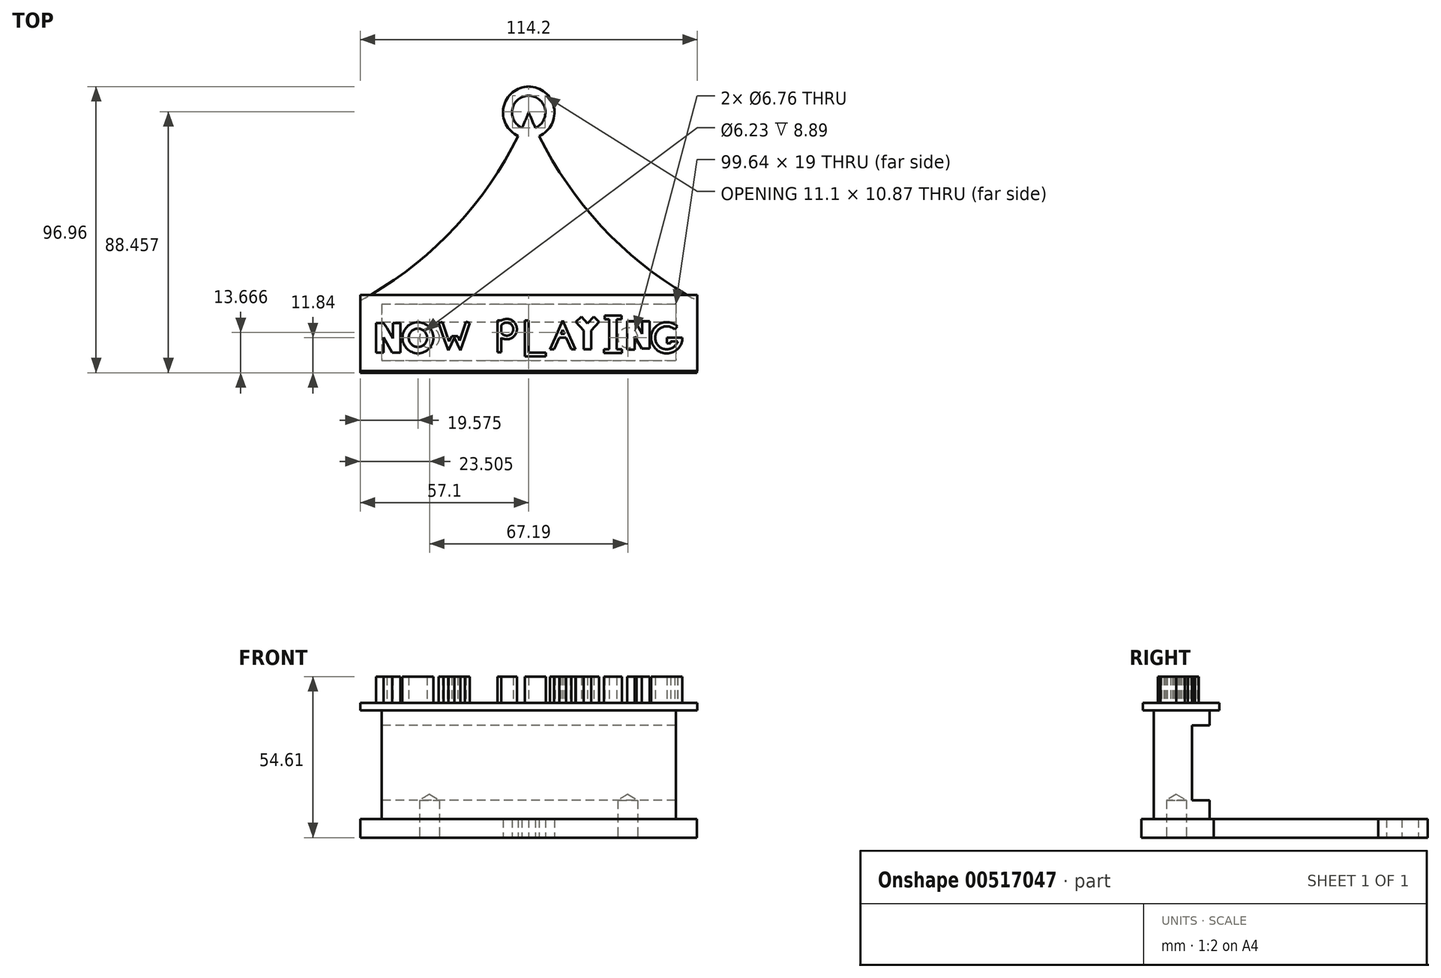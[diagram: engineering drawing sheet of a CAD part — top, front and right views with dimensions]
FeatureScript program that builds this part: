
annotation { "Feature Type Name" : "Feature", "Feature Type Description" : "" }
export const myFeature = defineFeature(function(context is Context, id is Id, definition is map)
    precondition{}
    {
        {
            var Q0;
            Q0=qCreatedBy(makeId("Top.planeOp"),FACE);
            var sketch = newSketch(context, id + "F0", { "sketchPlane" : qUnion([Q0])});
            skLineSegment(sketch, "E0", {"start": v(0, 0) * mm, "end": v(0, 12.6) * mm});
            skLineSegment(sketch, "E1", {"start": v(57, 12.6) * mm, "end": v(57, -11.84) * mm});
            skLineSegment(sketch, "E2", {"start": v(57, -11.84) * mm, "end": v(0, -11.84) * mm});
            skLineSegment(sketch, "E3", {"start": v(0, -11.84) * mm, "end": v(0, 0) * mm});
            skLineSegment(sketch, "E4.MirrorCS", {"start": v(-57, 12.6) * mm, "end": v(-57, -11.84) * mm});
            skLineSegment(sketch, "E5.MirrorCS", {"start": v(-57, -11.84) * mm, "end": v(0, -11.84) * mm});
            skLineSegment(sketch, "E6", {"start": v(0, 12.6) * mm, "end": v(0, 76.38) * mm});
            skArc(sketch, "E7", {"start": v(-57, 12.6) * mm, "mid": v(-25.97, 36.38) * mm, "end": v(-3.58, 68.42) * mm});
            skArc(sketch, "E8.MirrorCS", {"start": v(57, 12.6) * mm, "mid": v(25.97, 36.38) * mm, "end": v(3.58, 68.42) * mm});
            skArc(sketch, "E9", {"start": v(3.58, 68.42) * mm, "mid": v(0, 85.12) * mm, "end": v(-3.58, 68.42) * mm});
            skArc(sketch, "E10", {"start": v(2.26, 71.18) * mm, "mid": v(0, 82.05) * mm, "end": v(-2.26, 71.18) * mm});
            skPoint(sketch, "E11.MirrorCS.start.orphan", {"position": v(0, 12.6) * mm});
            skArc(sketch, "E12.trimOffspring", {"start": v(2.26, 71.18) * mm, "mid": v(1.1, 73.77) * mm, "end": v(0, 76.38) * mm});
            skArc(sketch, "E13.trimOffspring", {"start": v(-2.26, 71.18) * mm, "mid": v(-1.1, 73.77) * mm, "end": v(0, 76.38) * mm});
            skSolve(sketch);
        }
        {
            var Q0;
            Q0=makeQuery(id+"F0.imprint","IMPRINT",FACE,{"disambiguationData":[TD([[makeQuery(id+"F0.imprint","IMPRINT",EDGE,{"derivedFrom":sQuery(id+"F0.wireOp",EDGE,"E1")}),-1.0]])]});
            extrude(context, id + "F1", {"entities" : qUnion([Q0]), "depth" : 6.35 * mm, "offsetDistance" : 25.4 * mm});
        }
        {
            var Q0;
            Q0=makeQuery(id+"F1.opExtrude","CAP_FACE",FACE,{"disambiguationData":[OSD([sQuery(id+"F0.wireOp",EDGE,"E1"),sQuery(id+"F0.wireOp",EDGE,"E2"),sQuery(id+"F0.wireOp",EDGE,"E4.MirrorCS"),sQuery(id+"F0.wireOp",EDGE,"E5.MirrorCS"),sQuery(id+"F0.wireOp",EDGE,"E7"),sQuery(id+"F0.wireOp",EDGE,"E8.MirrorCS"),sQuery(id+"F0.wireOp",EDGE,"E9"),sQuery(id+"F0.wireOp",EDGE,"E10"),sQuery(id+"F0.wireOp",EDGE,"E12.trimOffspring"),sQuery(id+"F0.wireOp",EDGE,"E13.trimOffspring")])],"isStart":false});
            var sketch = newSketch(context, id + "F2", { "sketchPlane" : qUnion([Q0])});
            skLineSegment(sketch, "E14", {"start": v(0, 0) * mm, "end": v(0, 11.33) * mm});
            skLineSegment(sketch, "E15", {"start": v(0, 11.33) * mm, "end": v(-49.82, 11.33) * mm});
            skLineSegment(sketch, "E16", {"start": v(-49.82, 11.33) * mm, "end": v(-49.82, -7.67) * mm});
            skLineSegment(sketch, "E17", {"start": v(-49.82, -7.67) * mm, "end": v(0, -7.67) * mm});
            skLineSegment(sketch, "E18", {"start": v(0, -7.67) * mm, "end": v(0, 0) * mm});
            skLineSegment(sketch, "E19.MirrorCS", {"start": v(0, 11.33) * mm, "end": v(49.82, 11.33) * mm});
            skLineSegment(sketch, "E20.MirrorCS", {"start": v(49.82, 11.33) * mm, "end": v(49.82, -7.67) * mm});
            skLineSegment(sketch, "E21.MirrorCS", {"start": v(49.82, -7.67) * mm, "end": v(0, -7.67) * mm});
            skSolve(sketch);
        }
        {
            var Q0;
            Q0=makeQuery(id+"F2.imprint","IMPRINT",FACE,{"disambiguationData":[TD([[makeQuery(id+"F2.imprint","IMPRINT",EDGE,{"derivedFrom":sQuery(id+"F2.wireOp",EDGE,"E14")}),1.0]])]});
            var Q1;
            Q1=makeQuery(id+"F2.imprint","IMPRINT",FACE,{"disambiguationData":[TD([[makeQuery(id+"F2.imprint","IMPRINT",EDGE,{"derivedFrom":sQuery(id+"F2.wireOp",EDGE,"E14")}),-1.0]])]});
            extrude(context, id + "F3", {"entities" : qUnion([Q0, Q1]), "operationType" : NewBodyOperationType.ADD, "depth" : 6.35 * mm, "offsetDistance" : 25.4 * mm});
        }
        {
            var Q0;
            Q0=makeQuery(id+"F3.opExtrude","CAP_FACE",FACE,{"disambiguationData":[OSD([sQuery(id+"F2.wireOp",EDGE,"E15"),sQuery(id+"F2.wireOp",EDGE,"E16"),sQuery(id+"F2.wireOp",EDGE,"E17"),sQuery(id+"F2.wireOp",EDGE,"E19.MirrorCS"),sQuery(id+"F2.wireOp",EDGE,"E20.MirrorCS"),sQuery(id+"F2.wireOp",EDGE,"E21.MirrorCS")])],"isStart":false});
            var sketch = newSketch(context, id + "F4", { "sketchPlane" : qUnion([Q0])});
            skLineSegment(sketch, "E22", {"start": v(0, 0) * mm, "end": v(0, 5.26) * mm});
            skLineSegment(sketch, "E23", {"start": v(0, 5.26) * mm, "end": v(-49.82, 5.26) * mm});
            skLineSegment(sketch, "E24", {"start": v(-49.82, 5.26) * mm, "end": v(-49.82, -7.67) * mm});
            skLineSegment(sketch, "E25", {"start": v(-49.82, -7.67) * mm, "end": v(0, -7.67) * mm});
            skLineSegment(sketch, "E26", {"start": v(0, -7.67) * mm, "end": v(0, 0) * mm});
            skLineSegment(sketch, "E27.MirrorCS", {"start": v(0, 5.26) * mm, "end": v(49.82, 5.26) * mm});
            skLineSegment(sketch, "E28.MirrorCS", {"start": v(49.82, 5.26) * mm, "end": v(49.82, -7.67) * mm});
            skLineSegment(sketch, "E29.MirrorCS", {"start": v(49.82, -7.67) * mm, "end": v(0, -7.67) * mm});
            skSolve(sketch);
        }
        {
            var Q0;
            Q0=makeQuery(id+"F4.imprint","IMPRINT",FACE,{"disambiguationData":[TD([[makeQuery(id+"F4.imprint","IMPRINT",EDGE,{"derivedFrom":sQuery(id+"F4.wireOp",EDGE,"E22")}),1.0]])]});
            var Q1;
            Q1=makeQuery(id+"F4.imprint","IMPRINT",FACE,{"disambiguationData":[TD([[makeQuery(id+"F4.imprint","IMPRINT",EDGE,{"derivedFrom":sQuery(id+"F4.wireOp",EDGE,"E22")}),-1.0]])]});
            extrude(context, id + "F5", {"entities" : qUnion([Q0, Q1]), "operationType" : NewBodyOperationType.ADD, "depth" : 25.4 * mm, "offsetDistance" : 25.4 * mm});
        }
        {
            var Q0;
            Q0=makeQuery(id+"F1.opExtrude","CAP_FACE",FACE,{"disambiguationData":[OSD([sQuery(id+"F0.wireOp",EDGE,"E1"),sQuery(id+"F0.wireOp",EDGE,"E2"),sQuery(id+"F0.wireOp",EDGE,"E4.MirrorCS"),sQuery(id+"F0.wireOp",EDGE,"E5.MirrorCS"),sQuery(id+"F0.wireOp",EDGE,"E7"),sQuery(id+"F0.wireOp",EDGE,"E8.MirrorCS"),sQuery(id+"F0.wireOp",EDGE,"E9"),sQuery(id+"F0.wireOp",EDGE,"E10"),sQuery(id+"F0.wireOp",EDGE,"E12.trimOffspring"),sQuery(id+"F0.wireOp",EDGE,"E13.trimOffspring")])],"isStart":true});
            var sketch = newSketch(context, id + "F6", { "sketchPlane" : qUnion([Q0])});
            skPoint(sketch, "E30", {"position": v(0, 0) * mm});
            skPoint(sketch, "E31", {"position": v(33.6, 0) * mm});
            skPoint(sketch, "E32.MirrorP", {"position": v(-33.6, 0) * mm});
            skSolve(sketch);
        }
        {
            var Q0;
            Q0=sQuery(id+"F6.wireOp",VERTEX,"E31");
            var Q1;
            Q1=sQuery(id+"F6.wireOp",VERTEX,"E32.MirrorP");
            var Q2;
            Q2=makeQuery(id+"F1.opExtrude","SWEPT_BODY",BODY,{"disambiguationData":[OSD([sQuery(id+"F0.wireOp",EDGE,"E1"),sQuery(id+"F0.wireOp",EDGE,"E2"),sQuery(id+"F0.wireOp",EDGE,"E4.MirrorCS"),sQuery(id+"F0.wireOp",EDGE,"E5.MirrorCS"),sQuery(id+"F0.wireOp",EDGE,"E7"),sQuery(id+"F0.wireOp",EDGE,"E8.MirrorCS"),sQuery(id+"F0.wireOp",EDGE,"E9"),sQuery(id+"F0.wireOp",EDGE,"E10"),sQuery(id+"F0.wireOp",EDGE,"E12.trimOffspring"),sQuery(id+"F0.wireOp",EDGE,"E13.trimOffspring")])]});
            hole(context, id + "F7", {"style" : HoleStyle.SIMPLE, "endStyle" : HoleEndStyle.BLIND, "standardTappedOrClearance" : lookupTablePath({ "standard" : "ANSI", "fit" : "Normal (ASME)", "size" : "1/4", "type" : "Clearance" }), "standardBlindInLast" : lookupTablePath({ "fit" : "Free", "standard" : "ANSI", "size" : "1/4", "type" : "Clearance" }), "holeDiameter" : 6.76 * mm, "holeDepth" : 12.7 * mm, "isTappedThrough" : true, "tappedDepth" : 12.7 * mm, "tapClearance" : 3, "startFromSketch" : true, "locations" : qUnion([Q0, Q1]), "scope" : qUnion([Q2])});
        }
        {
            var Q0;
            Q0=makeQuery(id+"F5.opExtrude","CAP_FACE",FACE,{"disambiguationData":[OSD([sQuery(id+"F4.wireOp",EDGE,"E23"),sQuery(id+"F4.wireOp",EDGE,"E24"),sQuery(id+"F4.wireOp",EDGE,"E25"),sQuery(id+"F4.wireOp",EDGE,"E27.MirrorCS"),sQuery(id+"F4.wireOp",EDGE,"E28.MirrorCS"),sQuery(id+"F4.wireOp",EDGE,"E29.MirrorCS")])],"isStart":false});
            var sketch = newSketch(context, id + "F8", { "sketchPlane" : qUnion([Q0])});
            skLineSegment(sketch, "E33", {"start": v(0, 11.33) * mm, "end": v(-49.82, 11.33) * mm});
            skLineSegment(sketch, "E34", {"start": v(-49.82, 11.33) * mm, "end": v(-49.82, -7.67) * mm});
            skLineSegment(sketch, "E35", {"start": v(-49.82, -7.67) * mm, "end": v(0, -7.67) * mm});
            skLineSegment(sketch, "E36.MirrorCS", {"start": v(0, 11.33) * mm, "end": v(49.82, 11.33) * mm});
            skLineSegment(sketch, "E37.MirrorCS", {"start": v(49.82, 11.33) * mm, "end": v(49.82, -7.67) * mm});
            skLineSegment(sketch, "E38.MirrorCS", {"start": v(49.82, -7.67) * mm, "end": v(0, -7.67) * mm});
            skSolve(sketch);
        }
        {
            var Q0;
            {var subQ3=sQuery(id+"F8.wireOp",EDGE,"E33");Q0=makeQuery(id+"F8.imprint","IMPRINT",FACE,{"disambiguationData":[TD([[makeQuery(id+"F8.imprint","IMPRINT",EDGE,{"derivedFrom":subQ3}),1.0]])]});}
            var Q1;
            {var subQ3=sQuery(id+"F8.wireOp",EDGE,"E35");Q1=makeQuery(id+"F8.imprint","IMPRINT",FACE,{"disambiguationData":[TD([[makeQuery(id+"F8.imprint","IMPRINT",EDGE,{"derivedFrom":subQ3}),1.0]])]});}
            extrude(context, id + "F9", {"entities" : qUnion([Q0, Q1]), "operationType" : NewBodyOperationType.ADD, "depth" : 5.08 * mm, "offsetDistance" : 25.4 * mm});
        }
        {
            var Q0;
            Q0=makeQuery(id+"F9.opExtrude","CAP_FACE",FACE,{"disambiguationData":[OSD([sQuery(id+"F8.wireOp",EDGE,"E33"),sQuery(id+"F8.wireOp",EDGE,"E34"),sQuery(id+"F8.wireOp",EDGE,"E35"),sQuery(id+"F8.wireOp",EDGE,"E36.MirrorCS"),sQuery(id+"F8.wireOp",EDGE,"E37.MirrorCS"),sQuery(id+"F8.wireOp",EDGE,"E38.MirrorCS")])],"isStart":false});
            var sketch = newSketch(context, id + "F10", { "sketchPlane" : qUnion([Q0])});
            skPoint(sketch, "E39.endSnap0", {"position": v(0, 11.33) * mm});
            skLineSegment(sketch, "E40", {"start": v(0, 14.56) * mm, "end": v(-57.1, 14.56) * mm});
            skLineSegment(sketch, "E41", {"start": v(-57.1, 14.56) * mm, "end": v(-57.1, -11.31) * mm});
            skLineSegment(sketch, "E42", {"start": v(-57.1, -11.31) * mm, "end": v(0, -11.31) * mm});
            skLineSegment(sketch, "E43.MirrorCS", {"start": v(0, 14.56) * mm, "end": v(57.1, 14.56) * mm});
            skLineSegment(sketch, "E44.MirrorCS", {"start": v(57.1, 14.56) * mm, "end": v(57.1, -11.31) * mm});
            skLineSegment(sketch, "E45.MirrorCS", {"start": v(57.1, -11.31) * mm, "end": v(0, -11.31) * mm});
            skSolve(sketch);
        }
        {
            var Q0;
            Q0=makeQuery(id+"F10.imprint","IMPRINT",FACE,{"disambiguationData":[TD([[makeQuery(id+"F10.imprint","IMPRINT",EDGE,{"derivedFrom":sQuery(id+"F10.wireOp",EDGE,"E40")}),1.0]])]});
            var Q1;
            Q1=makeQuery(id+"F10.imprint","IMPRINT",FACE,{"disambiguationData":[TD([[makeQuery(id+"F10.imprint","IMPRINT",EDGE,{"derivedFrom":makeQuery(id+"F9.opExtrude","CAP_EDGE",EDGE,{"disambiguationData":[OSD([sQuery(id+"F8.wireOp",EDGE,"E34")])],"isStart":false})}),1.0]])]});
            extrude(context, id + "F11", {"entities" : qUnion([Q0, Q1]), "operationType" : NewBodyOperationType.ADD, "depth" : 2.54 * mm, "offsetDistance" : 25.4 * mm});
        }
        {
            var Q0;
            Q0=makeQuery(id+"F11.opExtrude","CAP_FACE",FACE,{"disambiguationData":[OSD([sQuery(id+"F10.wireOp",EDGE,"E40"),sQuery(id+"F10.wireOp",EDGE,"E41"),sQuery(id+"F10.wireOp",EDGE,"E42"),sQuery(id+"F10.wireOp",EDGE,"E43.MirrorCS"),sQuery(id+"F10.wireOp",EDGE,"E44.MirrorCS"),sQuery(id+"F10.wireOp",EDGE,"E45.MirrorCS")])],"isStart":false});
            var sketch = newSketch(context, id + "F12", { "sketchPlane" : qUnion([Q0])});
            skCircle(sketch, "E46", {"center": v(-37.52, 0) * mm, "radius": 5.25 * mm});
            skLineSegment(sketch, "E47", {"start": v(-28.85, 0) * mm, "end": v(-30.46, 5.06) * mm});
            skLineSegment(sketch, "E48", {"start": v(-28.85, 0) * mm, "end": v(-27.23, -4.23) * mm});
            skLineSegment(sketch, "E49", {"start": v(-27.23, -4.23) * mm, "end": v(-25.21, 0) * mm});
            skLineSegment(sketch, "E50.MirrorCS", {"start": v(-21.58, 0) * mm, "end": v(-19.97, 5.06) * mm});
            skLineSegment(sketch, "E51.MirrorCS", {"start": v(-21.58, 0) * mm, "end": v(-23.2, -4.23) * mm});
            skLineSegment(sketch, "E52.MirrorCS", {"start": v(-23.2, -4.23) * mm, "end": v(-25.21, 0) * mm});
            skArc(sketch, "E53", {"start": v(-9.27, 0) * mm, "mid": v(-3.98, 2.93) * mm, "end": v(-9.27, 5.86) * mm});
            skLineSegment(sketch, "E54", {"start": v(0, 0) * mm, "end": v(0, 5.87) * mm});
            skLineSegment(sketch, "E55", {"start": v(0, 5.87) * mm, "end": v(0, -5.04) * mm});
            skLineSegment(sketch, "E56", {"start": v(0, -5.04) * mm, "end": v(5.76, -5.04) * mm});
            skLineSegment(sketch, "E57", {"start": v(10.38, 0) * mm, "end": v(12.66, 0) * mm});
            skLineSegment(sketch, "E58", {"start": v(12.66, 0) * mm, "end": v(11.52, 0) * mm});
            skLineSegment(sketch, "E59", {"start": v(11.52, 5.86) * mm, "end": v(14.05, 0) * mm});
            skLineSegment(sketch, "E60", {"start": v(14.05, 0) * mm, "end": v(15.87, -3.83) * mm});
            skLineSegment(sketch, "E61.MirrorCS", {"start": v(11.52, 5.86) * mm, "end": v(9, 0) * mm});
            skLineSegment(sketch, "E62.MirrorCS", {"start": v(9, 0) * mm, "end": v(7.18, -3.83) * mm});
            skPoint(sketch, "E63.startSnap0", {"position": v(-3.98, 2.93) * mm});
            skLineSegment(sketch, "E64", {"start": v(27.28, -3.93) * mm, "end": v(25.49, -3.93) * mm});
            skLineSegment(sketch, "E65", {"start": v(27.28, 6.26) * mm, "end": v(25.7, 6.26) * mm});
            skLineSegment(sketch, "E66.MirrorCS", {"start": v(29.82, 6.26) * mm, "end": v(31.4, 6.26) * mm});
            skLineSegment(sketch, "E67.MirrorCS", {"start": v(29.82, -3.93) * mm, "end": v(31.6, -3.93) * mm});
            skLineSegment(sketch, "E68", {"start": v(46.77, 0) * mm, "end": v(50.43, 0) * mm});
            skArc(sketch, "E69", {"start": v(50.43, 3.85) * mm, "mid": v(41.9, -2.1) * mm, "end": v(52.08, 0) * mm});
            skLineSegment(sketch, "E70", {"start": v(46.77, 0) * mm, "end": v(52.08, 0) * mm});
            skLineSegment(sketch, "E71", {"start": v(52.08, 0) * mm, "end": v(46.77, 0) * mm});
            skLineSegment(sketch, "E72", {"start": v(46.77, 0) * mm, "end": v(46.77, -1.9) * mm});
            skLineSegment(sketch, "E73.0", {"start": v(-49.16, 0) * mm, "end": v(-49.16, 0.17) * mm});
            skLineSegment(sketch, "E74.0", {"start": v(-51.7, 0) * mm, "end": v(-51.7, -5.06) * mm});
            skLineSegment(sketch, "E75.0", {"start": v(-51.7, 0) * mm, "end": v(-51.7, 5.06) * mm});
            skLineSegment(sketch, "E76.0", {"start": v(-49.16, 0) * mm, "end": v(-49.16, -5.06) * mm});
            skLineSegment(sketch, "E77.0", {"start": v(-49.16, 0.17) * mm, "end": v(-46.24, -5.06) * mm});
            skLineSegment(sketch, "E78.0", {"start": v(-46.06, -0.17) * mm, "end": v(-46.06, 0) * mm});
            skLineSegment(sketch, "E79.MirrorCS", {"start": v(-46.06, 5.06) * mm, "end": v(-46.06, 0) * mm});
            skPoint(sketch, "E80.start.orphan", {"position": v(-50.43, 0) * mm});
            skPoint(sketch, "E81.MirrorCS.end.orphan", {"position": v(-50.43, -5.06) * mm});
            skLineSegment(sketch, "E82.0", {"start": v(-48.05, 3.4) * mm, "end": v(-46.06, -0.17) * mm});
            skLineSegment(sketch, "E83", {"start": v(-48.05, 3.4) * mm, "end": v(-49.16, 5.06) * mm});
            skLineSegment(sketch, "E84", {"start": v(-51.7, 5.06) * mm, "end": v(-49.16, 5.06) * mm});
            skLineSegment(sketch, "E85", {"start": v(-51.7, -5.06) * mm, "end": v(-49.16, -5.06) * mm});
            skLineSegment(sketch, "E86.0", {"start": v(-43.52, 5.06) * mm, "end": v(-43.52, 0) * mm});
            skLineSegment(sketch, "E87.0", {"start": v(-43.52, -5.06) * mm, "end": v(-43.52, 0) * mm});
            skLineSegment(sketch, "E88", {"start": v(-46.06, 5.06) * mm, "end": v(-43.52, 5.06) * mm});
            skLineSegment(sketch, "E89", {"start": v(-46.06, -5.06) * mm, "end": v(-43.52, -5.06) * mm});
            skPoint(sketch, "E90.start.orphan", {"position": v(-44.8, -5.06) * mm});
            skLineSegment(sketch, "E91", {"start": v(-46.24, -5.06) * mm, "end": v(-46.06, -5.06) * mm});
            skCircle(sketch, "E92", {"center": v(-37.52, 0) * mm, "radius": 3.11 * mm});
            skLineSegment(sketch, "E93.0", {"start": v(-27.64, 0.39) * mm, "end": v(-29.25, 5.44) * mm});
            skLineSegment(sketch, "E94.0", {"start": v(-27.66, 0.45) * mm, "end": v(-27.65, 0.42) * mm});
            skLineSegment(sketch, "E95", {"start": v(-27, -1.28) * mm, "end": v(-26.06, 0.57) * mm});
            skLineSegment(sketch, "E96", {"start": v(-26.06, 0.57) * mm, "end": v(-24.07, 0.55) * mm});
            skLineSegment(sketch, "E97", {"start": v(-19.97, 5.06) * mm, "end": v(-21.29, 5.48) * mm});
            skLineSegment(sketch, "E98", {"start": v(-21.29, 5.48) * mm, "end": v(-23.35, -0.96) * mm});
            skLineSegment(sketch, "E99", {"start": v(-30.46, 5.06) * mm, "end": v(-29.25, 5.44) * mm});
            skLineSegment(sketch, "E100.trimOffspring", {"start": v(-23.35, -0.96) * mm, "end": v(-24.07, 0.55) * mm});
            skLineSegment(sketch, "E101", {"start": v(-27.64, 0.39) * mm, "end": v(-27, -1.28) * mm});
            skLineSegment(sketch, "E102.0", {"start": v(-10.54, 5.86) * mm, "end": v(-10.54, -5.04) * mm});
            skLineSegment(sketch, "E103", {"start": v(-10.54, 5.86) * mm, "end": v(-9.27, 5.86) * mm});
            skLineSegment(sketch, "E104", {"start": v(-10.54, -5.04) * mm, "end": v(-9.27, -5.04) * mm});
            skArc(sketch, "E105", {"start": v(-9.27, 1.69) * mm, "mid": v(-5.23, 2.93) * mm, "end": v(-9.27, 4.18) * mm});
            skLineSegment(sketch, "E106.trimOffspring", {"start": v(-9.27, 0) * mm, "end": v(-9.27, -5.04) * mm});
            skLineSegment(sketch, "E107", {"start": v(-9.27, 4.18) * mm, "end": v(-9.27, 1.69) * mm});
            skLineSegment(sketch, "E108.0", {"start": v(-1.27, 5.87) * mm, "end": v(-1.27, -5.04) * mm});
            skLineSegment(sketch, "E109.0", {"start": v(1.27, -4.96) * mm, "end": v(1.27, -5.04) * mm});
            skLineSegment(sketch, "E110.0", {"start": v(0, -6.3) * mm, "end": v(5.76, -6.3) * mm});
            skLineSegment(sketch, "E111", {"start": v(-1.27, -6.3) * mm, "end": v(0, -6.3) * mm});
            skLineSegment(sketch, "E112", {"start": v(-1.27, 5.87) * mm, "end": v(0, 5.87) * mm});
            skLineSegment(sketch, "E113", {"start": v(5.76, -5.04) * mm, "end": v(5.76, -6.3) * mm});
            skLineSegment(sketch, "E114", {"start": v(-1.27, -5.04) * mm, "end": v(-1.27, -6.3) * mm});
            skLineSegment(sketch, "E115.trimOffspring", {"start": v(-10.54, -4.96) * mm, "end": v(-9.27, -4.96) * mm});
            skLineSegment(sketch, "E116.0", {"start": v(10.14, -0.54) * mm, "end": v(8.58, -3.83) * mm});
            skLineSegment(sketch, "E117.0", {"start": v(12.9, -0.54) * mm, "end": v(14.46, -3.83) * mm});
            skLineSegment(sketch, "E118", {"start": v(7.18, -3.83) * mm, "end": v(8.58, -3.83) * mm});
            skLineSegment(sketch, "E119", {"start": v(15.87, -3.83) * mm, "end": v(14.46, -3.83) * mm});
            skLineSegment(sketch, "E120.trimOffspring", {"start": v(10.92, 1.27) * mm, "end": v(12.12, 1.27) * mm});
            skLineSegment(sketch, "E121.trimOffspring", {"start": v(10.38, 0) * mm, "end": v(10.16, -0.5) * mm});
            skPoint(sketch, "E122.orphan", {"position": v(9, 0) * mm});
            skLineSegment(sketch, "E123.trimOffspring", {"start": v(12.66, 0) * mm, "end": v(12.88, -0.5) * mm});
            skLineSegment(sketch, "E124.trimOffspring", {"start": v(11.52, 2.65) * mm, "end": v(10.92, 1.27) * mm});
            skLineSegment(sketch, "E125.trimOffspring", {"start": v(11.52, 2.65) * mm, "end": v(12.12, 1.27) * mm});
            skLineSegment(sketch, "E126.0", {"start": v(18.64, 2.44) * mm, "end": v(18.64, -3.83) * mm});
            skLineSegment(sketch, "E127.0", {"start": v(21.18, 2.44) * mm, "end": v(21.18, -3.83) * mm});
            skLineSegment(sketch, "E128.0", {"start": v(18.64, 2.44) * mm, "end": v(15.94, 5.42) * mm});
            skLineSegment(sketch, "E129.0", {"start": v(21.18, 2.44) * mm, "end": v(23.88, 5.42) * mm});
            skLineSegment(sketch, "E130", {"start": v(15.94, 5.42) * mm, "end": v(17.82, 7.13) * mm});
            skLineSegment(sketch, "E131", {"start": v(22, 7.13) * mm, "end": v(23.88, 5.42) * mm});
            skLineSegment(sketch, "E132", {"start": v(18.64, -3.83) * mm, "end": v(21.18, -3.83) * mm});
            skPoint(sketch, "E133.orphan", {"position": v(16.88, 6.27) * mm});
            skLineSegment(sketch, "E134.trimOffspring", {"start": v(19.9, 4.82) * mm, "end": v(17.82, 7.13) * mm});
            skLineSegment(sketch, "E135.trimOffspring", {"start": v(19.9, 4.82) * mm, "end": v(22, 7.13) * mm});
            skPoint(sketch, "E63.end.orphan", {"position": v(22.94, 6.27) * mm});
            skPoint(sketch, "E136.MirrorCS.start.orphan", {"position": v(19.9, 2.93) * mm});
            skPoint(sketch, "E137.end.orphan", {"position": v(19.9, -3.83) * mm});
            skLineSegment(sketch, "E138.0", {"start": v(27.28, 6.26) * mm, "end": v(27.28, -3.93) * mm});
            skLineSegment(sketch, "E139.0", {"start": v(29.82, 6.26) * mm, "end": v(29.82, -3.93) * mm});
            skLineSegment(sketch, "E140.0", {"start": v(28.55, 7.53) * mm, "end": v(31.4, 7.53) * mm});
            skLineSegment(sketch, "E141.0", {"start": v(28.55, 7.53) * mm, "end": v(25.7, 7.53) * mm});
            skLineSegment(sketch, "E142.0", {"start": v(28.55, -5.2) * mm, "end": v(31.6, -5.2) * mm});
            skLineSegment(sketch, "E143", {"start": v(25.49, -3.93) * mm, "end": v(25.49, -5.2) * mm});
            skLineSegment(sketch, "E144", {"start": v(25.49, -5.2) * mm, "end": v(28.55, -5.2) * mm});
            skLineSegment(sketch, "E145", {"start": v(31.6, -3.93) * mm, "end": v(31.6, -5.2) * mm});
            skLineSegment(sketch, "E146", {"start": v(25.7, 7.53) * mm, "end": v(25.7, 6.26) * mm});
            skLineSegment(sketch, "E147", {"start": v(31.4, 7.53) * mm, "end": v(31.4, 6.26) * mm});
            skPoint(sketch, "E148.orphan", {"position": v(28.55, 6.26) * mm});
            skLineSegment(sketch, "E149.0", {"start": v(35.93, 0) * mm, "end": v(35.93, 0.49) * mm});
            skLineSegment(sketch, "E150.0", {"start": v(33.4, 0) * mm, "end": v(33.4, -4.04) * mm});
            skLineSegment(sketch, "E151.0", {"start": v(35.93, 0) * mm, "end": v(35.93, -4.04) * mm});
            skLineSegment(sketch, "E152.0", {"start": v(33.4, 0) * mm, "end": v(33.34, 5.64) * mm});
            skLineSegment(sketch, "E153.0", {"start": v(40.99, -3.63) * mm, "end": v(40.99, 5.67) * mm});
            skLineSegment(sketch, "E154.0", {"start": v(38.45, 1.29) * mm, "end": v(38.45, 5.67) * mm});
            skLineSegment(sketch, "E155.0", {"start": v(35.93, 0.49) * mm, "end": v(36.58, -0.62) * mm});
            skLineSegment(sketch, "E156.0", {"start": v(36.05, 5.64) * mm, "end": v(38.45, 1.29) * mm});
            skLineSegment(sketch, "E157.0", {"start": v(36.58, -0.62) * mm, "end": v(38.26, -3.63) * mm});
            skLineSegment(sketch, "E158.0", {"start": v(38.81, 0.62) * mm, "end": v(38.82, 0.6) * mm});
            skLineSegment(sketch, "E159", {"start": v(33.34, 5.64) * mm, "end": v(35.88, 5.64) * mm});
            skLineSegment(sketch, "E160", {"start": v(33.4, -4.04) * mm, "end": v(35.93, -4.04) * mm});
            skLineSegment(sketch, "E161", {"start": v(38.45, 5.67) * mm, "end": v(40.99, 5.67) * mm});
            skLineSegment(sketch, "E162", {"start": v(38.45, -3.63) * mm, "end": v(40.99, -3.63) * mm});
            skLineSegment(sketch, "E163", {"start": v(35.88, 5.64) * mm, "end": v(36.05, 5.64) * mm});
            skLineSegment(sketch, "E164", {"start": v(38.45, -3.63) * mm, "end": v(38.26, -3.63) * mm});
            skArc(sketch, "E165", {"start": v(49.46, 2.82) * mm, "mid": v(42.98, -0.92) * mm, "end": v(50.46, -1.27) * mm});
            skLineSegment(sketch, "E166.0", {"start": v(52.08, -1.27) * mm, "end": v(51.93, -1.27) * mm});
            skLineSegment(sketch, "E167.0", {"start": v(48.04, -1.27) * mm, "end": v(48.04, -1.9) * mm});
            skLineSegment(sketch, "E168", {"start": v(50.43, 3.85) * mm, "end": v(49.46, 2.82) * mm});
            skLineSegment(sketch, "E169", {"start": v(46.77, -1.9) * mm, "end": v(48.04, -1.9) * mm});
            skLineSegment(sketch, "E170.trimOffspring", {"start": v(50.46, -1.27) * mm, "end": v(48.04, -1.27) * mm});
            skLineSegment(sketch, "E171", {"start": v(11.51, 5.87) * mm, "end": v(7.18, -3.83) * mm});
            skLineSegment(sketch, "E172", {"start": v(10.38, 0) * mm, "end": v(8.58, -3.83) * mm});
            skLineSegment(sketch, "E173", {"start": v(11.52, 5.86) * mm, "end": v(15.87, -3.83) * mm});
            skLineSegment(sketch, "E174", {"start": v(14.46, -3.83) * mm, "end": v(15.87, -3.83) * mm});
            skLineSegment(sketch, "E175", {"start": v(14.46, -3.83) * mm, "end": v(12.66, 0) * mm});
            skLineSegment(sketch, "E176", {"start": v(12.66, 0) * mm, "end": v(10.38, 0) * mm});
            skSolve(sketch);
        }
        {
            var Q0;
            Q0=makeQuery(id+"F12.imprint","IMPRINT",FACE,{"disambiguationData":[TD([[makeQuery(id+"F12.imprint","IMPRINT",EDGE,{"derivedFrom":sQuery(id+"F12.wireOp",EDGE,"E59")}),-1.0]])]});
            var Q1;
            Q1=makeQuery(id+"F12.imprint","IMPRINT",FACE,{"disambiguationData":[TD([[makeQuery(id+"F12.imprint","IMPRINT",EDGE,{"derivedFrom":sQuery(id+"F12.wireOp",EDGE,"E126.0")}),1.0]])]});
            var Q2;
            Q2=makeQuery(id+"F12.imprint","IMPRINT",FACE,{"disambiguationData":[TD([[makeQuery(id+"F12.imprint","IMPRINT",EDGE,{"derivedFrom":sQuery(id+"F12.wireOp",EDGE,"E46")}),1.0]])]});
            var Q3;
            Q3=makeQuery(id+"F12.imprint","IMPRINT",FACE,{"disambiguationData":[TD([[makeQuery(id+"F12.imprint","IMPRINT",EDGE,{"derivedFrom":sQuery(id+"F12.wireOp",EDGE,"E73.0")}),1.0]])]});
            var Q4;
            Q4=makeQuery(id+"F12.imprint","IMPRINT",FACE,{"disambiguationData":[TD([[makeQuery(id+"F12.imprint","IMPRINT",EDGE,{"derivedFrom":sQuery(id+"F12.wireOp",EDGE,"E47")}),-1.0]])]});
            var Q5;
            {var subQ3=sQuery(id+"F12.wireOp",EDGE,"E53");Q5=makeQuery(id+"F12.imprint","IMPRINT",FACE,{"disambiguationData":[TD([[makeQuery(id+"F12.imprint","IMPRINT",EDGE,{"derivedFrom":subQ3}),1.0]])]});}
            var Q6;
            Q6=makeQuery(id+"F12.imprint","IMPRINT",FACE,{"disambiguationData":[TD([[makeQuery(id+"F12.imprint","IMPRINT",EDGE,{"derivedFrom":sQuery(id+"F12.wireOp",EDGE,"E108.0")}),1.0]])]});
            var Q7;
            Q7=makeQuery(id+"F12.imprint","IMPRINT",FACE,{"disambiguationData":[TD([[makeQuery(id+"F12.imprint","IMPRINT",EDGE,{"derivedFrom":sQuery(id+"F12.wireOp",EDGE,"E64")}),1.0]])]});
            var Q8;
            Q8=makeQuery(id+"F12.imprint","IMPRINT",FACE,{"disambiguationData":[TD([[makeQuery(id+"F12.imprint","IMPRINT",EDGE,{"derivedFrom":sQuery(id+"F12.wireOp",EDGE,"E149.0")}),1.0]])]});
            var Q9;
            {var subQ0=sQuery(id+"F12.wireOp",EDGE,"E72");Q9=makeQuery(id+"F12.imprint","IMPRINT",FACE,{"disambiguationData":[TD([[makeQuery(id+"F12.imprint","IMPRINT",EDGE,{"derivedFrom":subQ0}),1.0]])]});}
            extrude(context, id + "F13", {"entities" : qUnion([Q0, Q1, Q2, Q3, Q4, Q5, Q6, Q7, Q8, Q9]), "operationType" : NewBodyOperationType.ADD, "depth" : 8.9 * mm, "offsetDistance" : 25.4 * mm});
        }
    });
